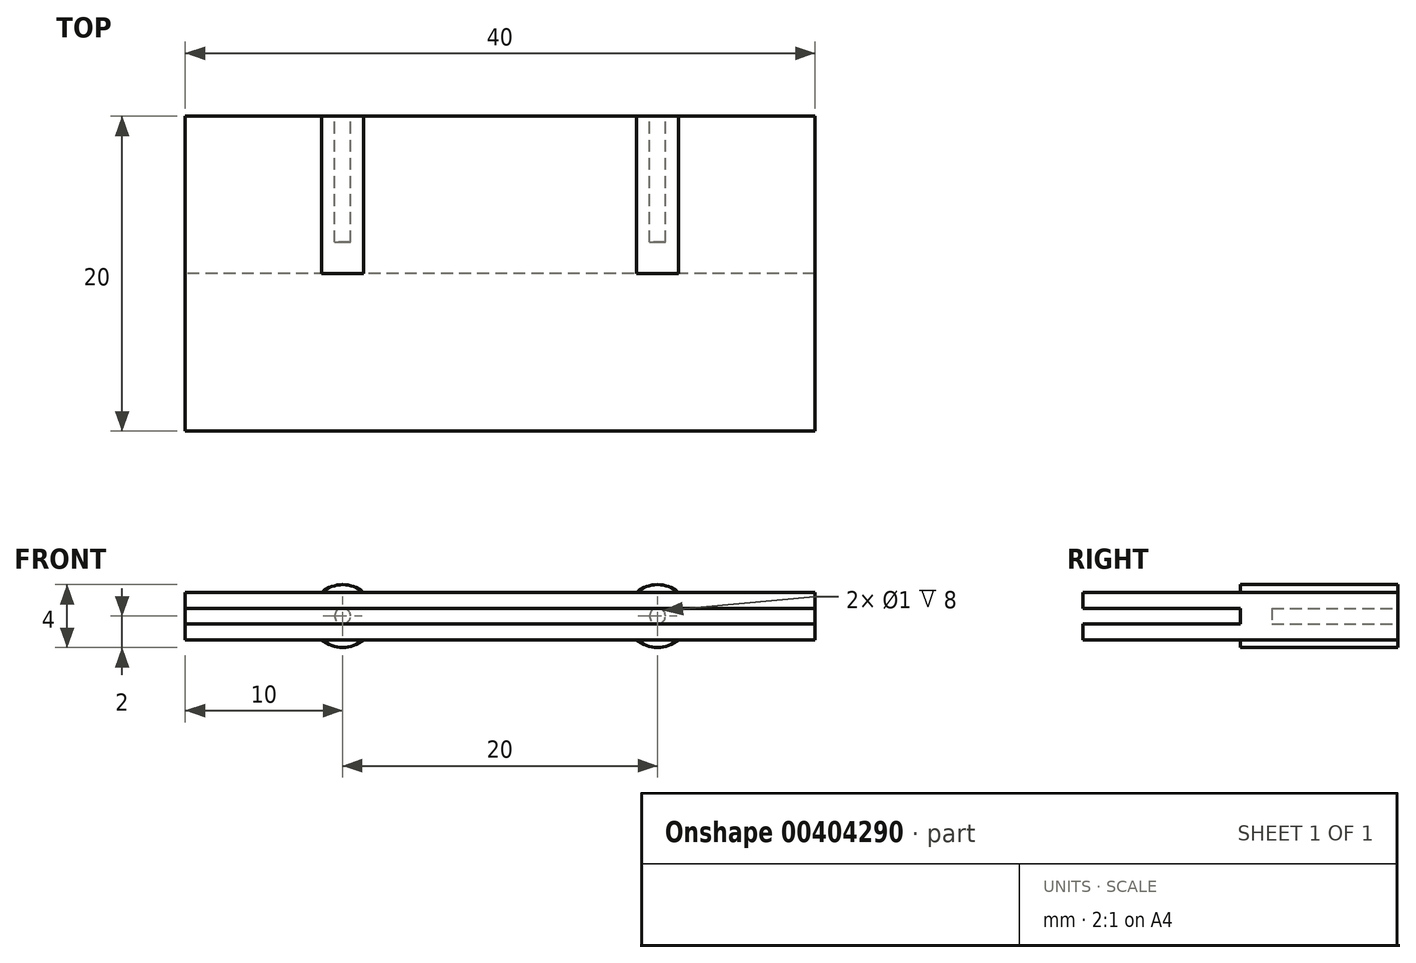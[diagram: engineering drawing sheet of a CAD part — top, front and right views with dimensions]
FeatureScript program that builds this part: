
annotation { "Feature Type Name" : "Feature", "Feature Type Description" : "" }
export const myFeature = defineFeature(function(context is Context, id is Id, definition is map)
    precondition{}
    {
        {
            var Q0;
            Q0=qCreatedBy(makeId("Top.planeOp"),FACE);
            var sketch = newSketch(context, id + "F0", { "sketchPlane" : qUnion([Q0])});
            skLineSegment(sketch, "E0.bottom", {"start": v(-20, -10) * mm, "end": v(20, -10) * mm});
            skLineSegment(sketch, "E0.top", {"start": v(-20, 10) * mm, "end": v(20, 10) * mm});
            skLineSegment(sketch, "E0.left", {"start": v(-20, -10) * mm, "end": v(-20, 10) * mm});
            skLineSegment(sketch, "E0.right", {"start": v(20, -10) * mm, "end": v(20, 10) * mm});
            skPoint(sketch, "E0.middle", {"position": v(0, 0) * mm});
            skSolve(sketch);
        }
        {
            var Q0;
            Q0=makeQuery(id+"F0.imprint","IMPRINT",FACE,{"disambiguationData":[TD([[makeQuery(id+"F0.imprint","IMPRINT",EDGE,{"derivedFrom":sQuery(id+"F0.wireOp",EDGE,"E0.bottom")}),1.0]])]});
            extrude(context, id + "F1", {"entities" : qUnion([Q0]), "depth" : 3 * mm});
        }
        {
            var Q0;
            Q0=makeQuery(id+"F1.opExtrude","SWEPT_FACE",FACE,{"disambiguationData":[OSD([sQuery(id+"F0.wireOp",EDGE,"E0.bottom")])]});
            var sketch = newSketch(context, id + "F2", { "sketchPlane" : qUnion([Q0])});
            skLineSegment(sketch, "E1", {"start": v(0, 3) * mm, "end": v(0, 0) * mm, "construction": true});
            skLineSegment(sketch, "E2.bottom", {"start": v(20, 2) * mm, "end": v(-20, 2) * mm});
            skLineSegment(sketch, "E2.top", {"start": v(20, 1) * mm, "end": v(-20, 1) * mm});
            skLineSegment(sketch, "E2.left", {"start": v(20, 2) * mm, "end": v(20, 1) * mm});
            skLineSegment(sketch, "E2.right", {"start": v(-20, 2) * mm, "end": v(-20, 1) * mm});
            skPoint(sketch, "E2.middle", {"position": v(0, 1.5) * mm});
            skSolve(sketch);
        }
        {
            var Q0;
            Q0=makeQuery(id+"F2.imprint","IMPRINT",FACE,{"disambiguationData":[TD([[makeQuery(id+"F2.imprint","IMPRINT",EDGE,{"derivedFrom":sQuery(id+"F2.wireOp",EDGE,"E2.bottom")}),1.0]])]});
            extrude(context, id + "F3", {"entities" : qUnion([Q0]), "operationType" : NewBodyOperationType.REMOVE, "oppositeDirection" : true, "depth" : 10 * mm});
        }
        {
            var Q0;
            Q0=makeQuery(id+"F1.opExtrude","SWEPT_FACE",FACE,{"disambiguationData":[OSD([sQuery(id+"F0.wireOp",EDGE,"E0.top")])]});
            var sketch = newSketch(context, id + "F4", { "sketchPlane" : qUnion([Q0])});
            skLineSegment(sketch, "E3", {"start": v(0, 3) * mm, "end": v(0, 0) * mm});
            skLineSegment(sketch, "E4.bottom", {"start": v(10, 3.5) * mm, "end": v(-10, 3.5) * mm});
            skLineSegment(sketch, "E4.top", {"start": v(10, -0.5) * mm, "end": v(-10, -0.5) * mm});
            skLineSegment(sketch, "E4.left", {"start": v(10, 3.5) * mm, "end": v(10, -0.5) * mm});
            skLineSegment(sketch, "E4.right", {"start": v(-10, 3.5) * mm, "end": v(-10, -0.5) * mm});
            skPoint(sketch, "E4.middle", {"position": v(0, 1.5) * mm});
            skCircle(sketch, "E5", {"center": v(10, 1.5) * mm, "radius": 0.5 * mm});
            skCircle(sketch, "E6", {"center": v(10, 1.5) * mm, "radius": 2 * mm});
            skCircle(sketch, "E7", {"center": v(-10, 1.5) * mm, "radius": 0.5 * mm});
            skCircle(sketch, "E8", {"center": v(-10, 1.5) * mm, "radius": 2 * mm});
            skLineSegment(sketch, "E9", {"start": v(-10, 1) * mm, "end": v(10, 1) * mm});
            skSolve(sketch);
        }
        {
            var Q0;
            {var subQ0=sQuery(id+"F4.wireOp",EDGE,"E6");var subQ3=makeQuery(id+"F1.opExtrude","CAP_EDGE",EDGE,{"disambiguationData":[OSD([sQuery(id+"F0.wireOp",EDGE,"E0.top")])],"isStart":false});var subQ5=makeQuery(id+"F4.imprint","INTERSECT",VERTEX,{"disambiguationData":[OD(0.0)],"derivedFrom":[subQ3,subQ0]});Q0=makeQuery(id+"F4.imprint","IMPRINT",FACE,{"disambiguationData":[TD([[makeQuery(id+"F4.imprint","IMPRINT",EDGE,{"disambiguationData":[TD([[subQ5,-1.0]])],"derivedFrom":subQ3}),-1.0]])]});}
            var Q1;
            {var subQ1=sQuery(id+"F4.wireOp",EDGE,"E4.left");var subQ3=makeQuery(id+"F1.opExtrude","CAP_EDGE",EDGE,{"disambiguationData":[OSD([sQuery(id+"F0.wireOp",EDGE,"E0.top")])],"isStart":false});var subQ4=makeQuery(id+"F4.imprint","INTERSECT",VERTEX,{"derivedFrom":[subQ3,subQ1]});Q1=makeQuery(id+"F4.imprint","IMPRINT",FACE,{"disambiguationData":[TD([[makeQuery(id+"F4.imprint","IMPRINT",EDGE,{"disambiguationData":[TD([[subQ4,-1.0]])],"derivedFrom":subQ3}),-1.0]])]});}
            var Q2;
            {var subQ1=sQuery(id+"F4.wireOp",EDGE,"E4.left");var subQ3=makeQuery(id+"F1.opExtrude","CAP_EDGE",EDGE,{"disambiguationData":[OSD([sQuery(id+"F0.wireOp",EDGE,"E0.top")])],"isStart":true});var subQ4=makeQuery(id+"F4.imprint","INTERSECT",VERTEX,{"derivedFrom":[subQ3,subQ1]});Q2=makeQuery(id+"F4.imprint","IMPRINT",FACE,{"disambiguationData":[TD([[makeQuery(id+"F4.imprint","IMPRINT",EDGE,{"disambiguationData":[TD([[subQ4,-1.0]])],"derivedFrom":subQ3}),1.0]])]});}
            var Q3;
            {var subQ0=sQuery(id+"F4.wireOp",EDGE,"E6");var subQ3=makeQuery(id+"F1.opExtrude","CAP_EDGE",EDGE,{"disambiguationData":[OSD([sQuery(id+"F0.wireOp",EDGE,"E0.top")])],"isStart":true});var subQ5=makeQuery(id+"F4.imprint","INTERSECT",VERTEX,{"disambiguationData":[OD(0.0)],"derivedFrom":[subQ3,subQ0]});Q3=makeQuery(id+"F4.imprint","IMPRINT",FACE,{"disambiguationData":[TD([[makeQuery(id+"F4.imprint","IMPRINT",EDGE,{"disambiguationData":[TD([[subQ5,-1.0]])],"derivedFrom":subQ3}),1.0]])]});}
            var Q4;
            {var subQ0=sQuery(id+"F4.wireOp",EDGE,"E8");var subQ3=makeQuery(id+"F1.opExtrude","CAP_EDGE",EDGE,{"disambiguationData":[OSD([sQuery(id+"F0.wireOp",EDGE,"E0.top")])],"isStart":true});var subQ5=makeQuery(id+"F4.imprint","INTERSECT",VERTEX,{"disambiguationData":[OD(0.0)],"derivedFrom":[subQ3,subQ0]});Q4=makeQuery(id+"F4.imprint","IMPRINT",FACE,{"disambiguationData":[TD([[makeQuery(id+"F4.imprint","IMPRINT",EDGE,{"disambiguationData":[TD([[subQ5,1.0]])],"derivedFrom":subQ3}),1.0]])]});}
            var Q5;
            {var subQ1=sQuery(id+"F4.wireOp",EDGE,"E4.right");var subQ3=makeQuery(id+"F1.opExtrude","CAP_EDGE",EDGE,{"disambiguationData":[OSD([sQuery(id+"F0.wireOp",EDGE,"E0.top")])],"isStart":true});var subQ4=makeQuery(id+"F4.imprint","INTERSECT",VERTEX,{"derivedFrom":[subQ3,subQ1]});Q5=makeQuery(id+"F4.imprint","IMPRINT",FACE,{"disambiguationData":[TD([[makeQuery(id+"F4.imprint","IMPRINT",EDGE,{"disambiguationData":[TD([[subQ4,1.0]])],"derivedFrom":subQ3}),1.0]])]});}
            var Q6;
            {var subQ0=sQuery(id+"F4.wireOp",EDGE,"E8");var subQ3=makeQuery(id+"F1.opExtrude","CAP_EDGE",EDGE,{"disambiguationData":[OSD([sQuery(id+"F0.wireOp",EDGE,"E0.top")])],"isStart":false});var subQ5=makeQuery(id+"F4.imprint","INTERSECT",VERTEX,{"disambiguationData":[OD(0.0)],"derivedFrom":[subQ3,subQ0]});Q6=makeQuery(id+"F4.imprint","IMPRINT",FACE,{"disambiguationData":[TD([[makeQuery(id+"F4.imprint","IMPRINT",EDGE,{"disambiguationData":[TD([[subQ5,1.0]])],"derivedFrom":subQ3}),-1.0]])]});}
            var Q7;
            {var subQ1=sQuery(id+"F4.wireOp",EDGE,"E4.right");var subQ3=makeQuery(id+"F1.opExtrude","CAP_EDGE",EDGE,{"disambiguationData":[OSD([sQuery(id+"F0.wireOp",EDGE,"E0.top")])],"isStart":false});var subQ4=makeQuery(id+"F4.imprint","INTERSECT",VERTEX,{"derivedFrom":[subQ3,subQ1]});Q7=makeQuery(id+"F4.imprint","IMPRINT",FACE,{"disambiguationData":[TD([[makeQuery(id+"F4.imprint","IMPRINT",EDGE,{"disambiguationData":[TD([[subQ4,1.0]])],"derivedFrom":subQ3}),-1.0]])]});}
            extrude(context, id + "F5", {"entities" : qUnion([Q0, Q1, Q2, Q3, Q4, Q5, Q6, Q7]), "operationType" : NewBodyOperationType.ADD, "depth" : -10 * mm});
        }
        {
            var Q0;
            {var subQ0=sQuery(id+"F4.wireOp",EDGE,"E7");var subQ1=sQuery(id+"F4.wireOp",EDGE,"E4.right");var subQ3=makeQuery(id+"F4.imprint","INTERSECT",VERTEX,{"derivedFrom":[subQ1,subQ0]});Q0=makeQuery(id+"F4.imprint","IMPRINT",FACE,{"disambiguationData":[TD([[makeQuery(id+"F4.imprint","IMPRINT",EDGE,{"disambiguationData":[TD([[subQ3,-1.0]])],"derivedFrom":subQ1}),-1.0]])]});}
            var Q1;
            {var subQ0=sQuery(id+"F4.wireOp",EDGE,"E7");var subQ1=sQuery(id+"F4.wireOp",EDGE,"E4.right");var subQ3=makeQuery(id+"F4.imprint","INTERSECT",VERTEX,{"derivedFrom":[subQ1,subQ0]});Q1=makeQuery(id+"F4.imprint","IMPRINT",FACE,{"disambiguationData":[TD([[makeQuery(id+"F4.imprint","IMPRINT",EDGE,{"disambiguationData":[TD([[subQ3,-1.0]])],"derivedFrom":subQ1}),1.0]])]});}
            var Q2;
            {var subQ0=sQuery(id+"F4.wireOp",EDGE,"E5");var subQ1=sQuery(id+"F4.wireOp",EDGE,"E4.left");var subQ3=makeQuery(id+"F4.imprint","INTERSECT",VERTEX,{"derivedFrom":[subQ1,subQ0]});Q2=makeQuery(id+"F4.imprint","IMPRINT",FACE,{"disambiguationData":[TD([[makeQuery(id+"F4.imprint","IMPRINT",EDGE,{"disambiguationData":[TD([[subQ3,-1.0]])],"derivedFrom":subQ1}),1.0]])]});}
            var Q3;
            {var subQ0=sQuery(id+"F4.wireOp",EDGE,"E5");var subQ1=sQuery(id+"F4.wireOp",EDGE,"E4.left");var subQ3=makeQuery(id+"F4.imprint","INTERSECT",VERTEX,{"derivedFrom":[subQ1,subQ0]});Q3=makeQuery(id+"F4.imprint","IMPRINT",FACE,{"disambiguationData":[TD([[makeQuery(id+"F4.imprint","IMPRINT",EDGE,{"disambiguationData":[TD([[subQ3,-1.0]])],"derivedFrom":subQ1}),-1.0]])]});}
            extrude(context, id + "F6", {"entities" : qUnion([Q0, Q1, Q2, Q3]), "operationType" : NewBodyOperationType.REMOVE, "oppositeDirection" : true, "depth" : 8 * mm});
        }
    });
